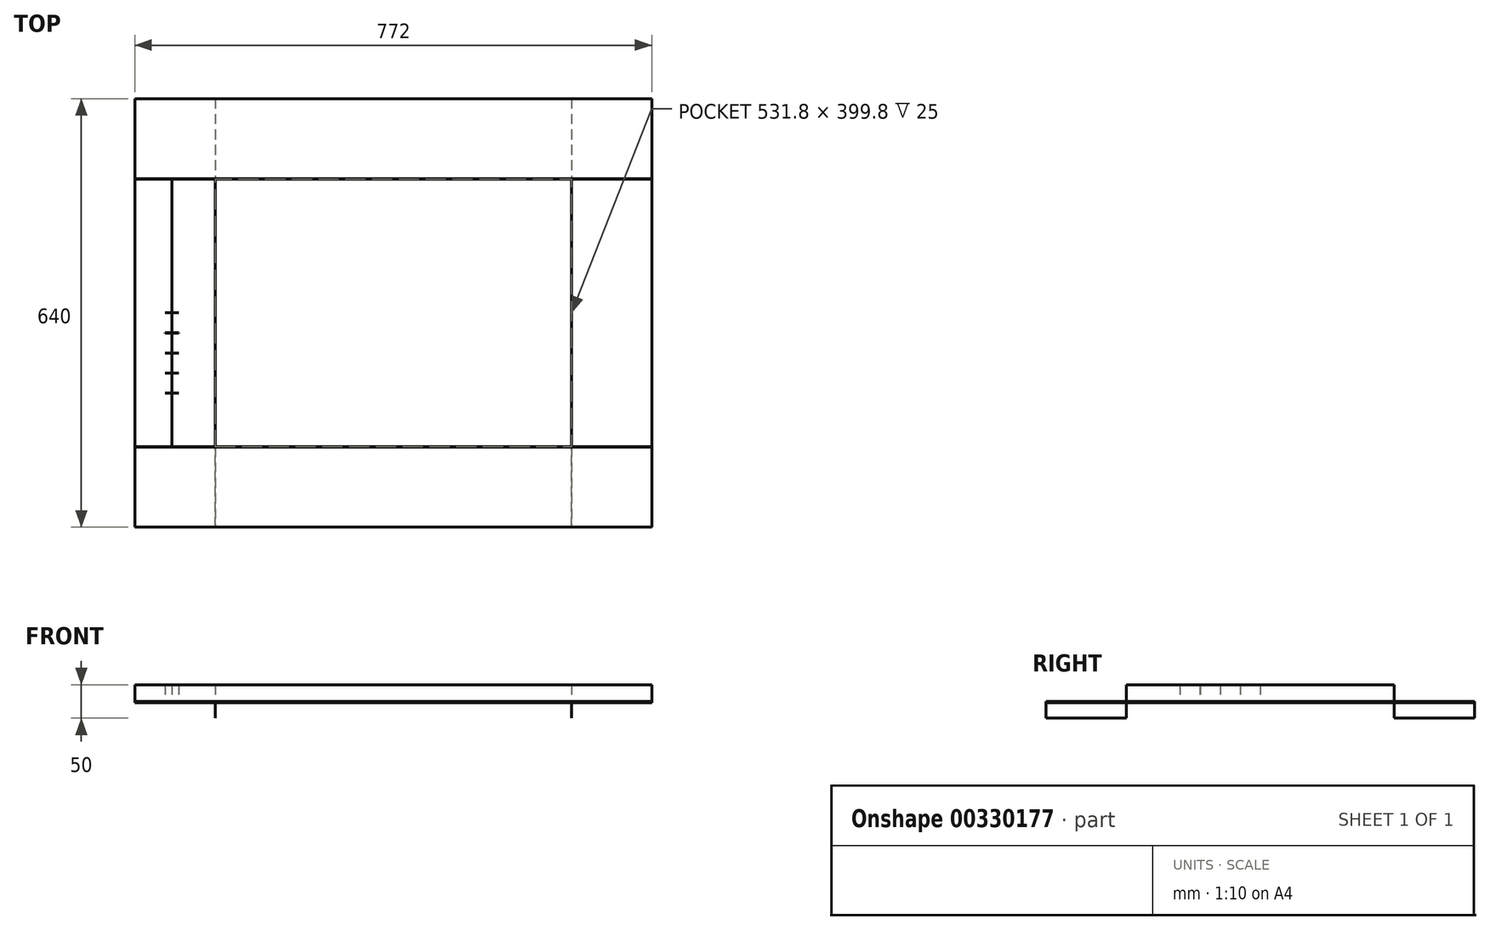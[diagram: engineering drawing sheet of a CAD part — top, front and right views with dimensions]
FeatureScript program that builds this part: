
annotation { "Feature Type Name" : "Feature", "Feature Type Description" : "" }
export const myFeature = defineFeature(function(context is Context, id is Id, definition is map)
    precondition{}
    {
        {
            var Q0;
            Q0=qCreatedBy(makeId("Top.planeOp"),FACE);
            var sketch = newSketch(context, id + "F0", { "sketchPlane" : qUnion([Q0])});
            skLineSegment(sketch, "E0.bottom", {"start": v(0, 0) * mm, "end": v(772, 0) * mm});
            skLineSegment(sketch, "E0.top", {"start": v(0, 640) * mm, "end": v(772, 640) * mm});
            skLineSegment(sketch, "E0.left", {"start": v(0, 0) * mm, "end": v(0, 640) * mm});
            skLineSegment(sketch, "E0.right", {"start": v(772, 0) * mm, "end": v(772, 640) * mm});
            skSolve(sketch);
        }
        {
            var Q0;
            Q0=makeQuery(id+"F0.imprint","IMPRINT",FACE,{"disambiguationData":[TD([[makeQuery(id+"F0.imprint","IMPRINT",EDGE,{"derivedFrom":sQuery(id+"F0.wireOp",EDGE,"E0.bottom")}),1.0]])]});
            extrude(context, id + "F1", {"entities" : qUnion([Q0]), "depth" : 2 * mm});
        }
        {
            var Q0;
            Q0=makeQuery(id+"F1.opExtrude","CAP_FACE",FACE,{"disambiguationData":[OSD([sQuery(id+"F0.wireOp",EDGE,"E0.bottom"),sQuery(id+"F0.wireOp",EDGE,"E0.top"),sQuery(id+"F0.wireOp",EDGE,"E0.left"),sQuery(id+"F0.wireOp",EDGE,"E0.right")])],"isStart":false});
            var sketch = newSketch(context, id + "F2", { "sketchPlane" : qUnion([Q0])});
            skLineSegment(sketch, "E1", {"start": v(0, 520.1) * mm, "end": v(772, 520.1) * mm});
            skLineSegment(sketch, "E2", {"start": v(0, 519.9) * mm, "end": v(772, 519.9) * mm});
            skLineSegment(sketch, "E3", {"start": v(0, 119.9) * mm, "end": v(772, 119.9) * mm});
            skLineSegment(sketch, "E4", {"start": v(0, 120.1) * mm, "end": v(772, 120.1) * mm});
            skLineSegment(sketch, "E5", {"start": v(652.1, 640) * mm, "end": v(652.1, 0) * mm});
            skLineSegment(sketch, "E6", {"start": v(119.9, 640) * mm, "end": v(119.9, 0) * mm});
            skLineSegment(sketch, "E7", {"start": v(120.1, 519.9) * mm, "end": v(120.1, 119.9) * mm});
            skLineSegment(sketch, "E8", {"start": v(651.9, 519.9) * mm, "end": v(651.9, 119.9) * mm});
            skLineSegment(sketch, "E9", {"start": v(120.15, 640) * mm, "end": v(120.15, 519.9) * mm});
            skLineSegment(sketch, "E10", {"start": v(651.85, 640) * mm, "end": v(651.85, 520.1) * mm});
            skLineSegment(sketch, "E11", {"start": v(120.15, 0) * mm, "end": v(120.15, 119.9) * mm});
            skLineSegment(sketch, "E12", {"start": v(651.85, 0) * mm, "end": v(651.85, 119.9) * mm});
            skLineSegment(sketch, "E13", {"start": v(55.2, 519.9) * mm, "end": v(55.2, 119.9) * mm});
            skLineSegment(sketch, "E14", {"start": v(55, 519.9) * mm, "end": v(55, 119.9) * mm});
            skLineSegment(sketch, "E15", {"start": v(45.2, 470.1) * mm, "end": v(45.2, 470.3) * mm});
            skLineSegment(sketch, "E16", {"start": v(65.2, 470.1) * mm, "end": v(65.2, 470.3) * mm});
            skLineSegment(sketch, "E17.1.0.2", {"start": v(65.2, 440.1) * mm, "end": v(65.2, 440.3) * mm});
            skLineSegment(sketch, "E17.1.0.3", {"start": v(45.2, 440.1) * mm, "end": v(45.2, 440.3) * mm});
            skLineSegment(sketch, "E17.2.0.2", {"start": v(65.2, 410.1) * mm, "end": v(65.2, 410.3) * mm});
            skLineSegment(sketch, "E17.2.0.3", {"start": v(45.2, 410.1) * mm, "end": v(45.2, 410.3) * mm});
            skLineSegment(sketch, "E17.3.0.2", {"start": v(65.2, 380.1) * mm, "end": v(65.2, 380.3) * mm});
            skLineSegment(sketch, "E17.3.0.3", {"start": v(45.2, 380.1) * mm, "end": v(45.2, 380.3) * mm});
            skLineSegment(sketch, "E17.4.0.2", {"start": v(65.2, 350.1) * mm, "end": v(65.2, 350.3) * mm});
            skLineSegment(sketch, "E17.4.0.3", {"start": v(45.2, 350.1) * mm, "end": v(45.2, 350.3) * mm});
            skLineSegment(sketch, "E17.5.0.2", {"start": v(65.2, 320.1) * mm, "end": v(65.2, 320.3) * mm});
            skLineSegment(sketch, "E17.5.0.3", {"start": v(45.2, 320.1) * mm, "end": v(45.2, 320.3) * mm});
            skLineSegment(sketch, "E17.6.0.2", {"start": v(65.2, 290.1) * mm, "end": v(65.2, 290.3) * mm});
            skLineSegment(sketch, "E17.6.0.3", {"start": v(45.2, 290.1) * mm, "end": v(45.2, 290.3) * mm});
            skLineSegment(sketch, "E17.7.0.2", {"start": v(65.2, 260.1) * mm, "end": v(65.2, 260.3) * mm});
            skLineSegment(sketch, "E17.7.0.3", {"start": v(45.2, 260.1) * mm, "end": v(45.2, 260.3) * mm});
            skLineSegment(sketch, "E17.8.0.2", {"start": v(65.2, 230.1) * mm, "end": v(65.2, 230.3) * mm});
            skLineSegment(sketch, "E17.8.0.3", {"start": v(45.2, 230.1) * mm, "end": v(45.2, 230.3) * mm});
            skLineSegment(sketch, "E17.9.0.2", {"start": v(65.2, 200.1) * mm, "end": v(65.2, 200.3) * mm});
            skLineSegment(sketch, "E17.9.0.3", {"start": v(45.2, 200.1) * mm, "end": v(45.2, 200.3) * mm});
            skLineSegment(sketch, "E17.direction1", {"start": v(45.2, 470.3) * mm, "end": v(45.2, 440.3) * mm, "construction": true});
            skLineSegment(sketch, "E18", {"start": v(55, 150.54) * mm, "end": v(55.2, 150.54) * mm});
            skLineSegment(sketch, "E19", {"start": v(45.2, 200.3) * mm, "end": v(65.2, 200.3) * mm});
            skLineSegment(sketch, "E20", {"start": v(45.2, 200.1) * mm, "end": v(65.2, 200.1) * mm});
            skLineSegment(sketch, "E21", {"start": v(45.2, 230.3) * mm, "end": v(65.2, 230.3) * mm});
            skLineSegment(sketch, "E22", {"start": v(65.2, 230.1) * mm, "end": v(45.2, 230.1) * mm});
            skLineSegment(sketch, "E23", {"start": v(45.2, 260.3) * mm, "end": v(65.2, 260.3) * mm});
            skLineSegment(sketch, "E24", {"start": v(65.2, 260.1) * mm, "end": v(45.2, 260.1) * mm});
            skLineSegment(sketch, "E25", {"start": v(45.2, 290.3) * mm, "end": v(65.2, 290.3) * mm});
            skLineSegment(sketch, "E26", {"start": v(65.2, 290.1) * mm, "end": v(45.2, 290.1) * mm});
            skLineSegment(sketch, "E27", {"start": v(45.2, 320.3) * mm, "end": v(65.2, 320.3) * mm});
            skLineSegment(sketch, "E28", {"start": v(45.2, 320.1) * mm, "end": v(65.2, 320.1) * mm});
            skSolve(sketch);
        }
        {
            var Q0;
            {var subQ0=sQuery(id+"F2.wireOp",EDGE,"E10");Q0=makeQuery(id+"F2.imprint","IMPRINT",FACE,{"disambiguationData":[TD([[makeQuery(id+"F2.imprint","IMPRINT",EDGE,{"derivedFrom":subQ0}),1.0]])]});}
            var Q1;
            {var subQ0=sQuery(id+"F2.wireOp",EDGE,"E6");var subQ1=sQuery(id+"F2.wireOp",EDGE,"E1");var subQ2=makeQuery(id+"F2.imprint","INTERSECT",VERTEX,{"derivedFrom":[subQ1,subQ0]});Q1=makeQuery(id+"F2.imprint","IMPRINT",FACE,{"disambiguationData":[TD([[makeQuery(id+"F2.imprint","IMPRINT",EDGE,{"disambiguationData":[TD([[subQ2,-1.0]])],"derivedFrom":subQ1}),1.0]])]});}
            var Q2;
            {var subQ0=sQuery(id+"F2.wireOp",EDGE,"E11");Q2=makeQuery(id+"F2.imprint","IMPRINT",FACE,{"disambiguationData":[TD([[makeQuery(id+"F2.imprint","IMPRINT",EDGE,{"derivedFrom":subQ0}),1.0]])]});}
            var Q3;
            {var subQ6=sQuery(id+"F2.wireOp",EDGE,"E12");Q3=makeQuery(id+"F2.imprint","IMPRINT",FACE,{"disambiguationData":[TD([[makeQuery(id+"F2.imprint","IMPRINT",EDGE,{"derivedFrom":subQ6}),-1.0]])]});}
            extrude(context, id + "F3", {"entities" : qUnion([Q0, Q1, Q2, Q3]), "operationType" : NewBodyOperationType.ADD, "oppositeDirection" : true, "depth" : 25 * mm});
        }
        {
            var Q0;
            {var subQ5=makeQuery(id+"F1.opExtrude","CAP_EDGE",EDGE,{"disambiguationData":[OSD([sQuery(id+"F0.wireOp",EDGE,"E0.left")])],"isStart":false});var subQ7=sQuery(id+"F2.wireOp",EDGE,"E1");var subQ8=makeQuery(id+"F2.imprint","INTERSECT",VERTEX,{"derivedFrom":[subQ5,subQ7]});Q0=makeQuery(id+"F2.imprint","IMPRINT",FACE,{"disambiguationData":[TD([[makeQuery(id+"F2.imprint","IMPRINT",EDGE,{"disambiguationData":[TD([[subQ8,-1.0]])],"derivedFrom":subQ7}),-1.0]])]});}
            var Q1;
            {var subQ6=sQuery(id+"F2.wireOp",EDGE,"E1");var subQ8=makeQuery(id+"F2.imprint","INTERSECT",VERTEX,{"derivedFrom":[subQ6,sQuery(id+"F2.wireOp",EDGE,"E10")]});Q1=makeQuery(id+"F2.imprint","IMPRINT",FACE,{"disambiguationData":[TD([[makeQuery(id+"F2.imprint","IMPRINT",EDGE,{"disambiguationData":[TD([[subQ8,1.0]])],"derivedFrom":subQ6}),-1.0]])]});}
            extrude(context, id + "F4", {"entities" : qUnion([Q0, Q1]), "operationType" : NewBodyOperationType.ADD, "depth" : 25 * mm});
        }
        {
            var Q0;
            {var subQ0=sQuery(id+"F2.wireOp",EDGE,"E1");var subQ1=makeQuery(id+"F1.opExtrude","CAP_EDGE",EDGE,{"disambiguationData":[OSD([sQuery(id+"F0.wireOp",EDGE,"E0.right")])],"isStart":false});var subQ2=makeQuery(id+"F2.imprint","INTERSECT",VERTEX,{"derivedFrom":[subQ1,subQ0]});Q0=makeQuery(id+"F2.imprint","IMPRINT",FACE,{"disambiguationData":[TD([[makeQuery(id+"F2.imprint","IMPRINT",EDGE,{"disambiguationData":[TD([[subQ2,1.0]])],"derivedFrom":subQ0}),-1.0]])]});}
            var Q1;
            {var subQ0=sQuery(id+"F2.wireOp",EDGE,"E8");var subQ1=sQuery(id+"F2.wireOp",EDGE,"E2");var subQ2=makeQuery(id+"F2.imprint","INTERSECT",VERTEX,{"derivedFrom":[subQ1,subQ0]});Q1=makeQuery(id+"F2.imprint","IMPRINT",FACE,{"disambiguationData":[TD([[makeQuery(id+"F2.imprint","IMPRINT",EDGE,{"disambiguationData":[TD([[subQ2,-1.0]])],"derivedFrom":subQ1}),-1.0]])]});}
            extrude(context, id + "F5", {"entities" : qUnion([Q0, Q1]), "operationType" : NewBodyOperationType.ADD, "depth" : 25 * mm});
        }
        {
            var Q0;
            {var subQ0=sQuery(id+"F2.wireOp",EDGE,"E3");var subQ1=makeQuery(id+"F1.opExtrude","CAP_EDGE",EDGE,{"disambiguationData":[OSD([sQuery(id+"F0.wireOp",EDGE,"E0.right")])],"isStart":false});var subQ2=makeQuery(id+"F2.imprint","INTERSECT",VERTEX,{"derivedFrom":[subQ1,subQ0]});Q0=makeQuery(id+"F2.imprint","IMPRINT",FACE,{"disambiguationData":[TD([[makeQuery(id+"F2.imprint","IMPRINT",EDGE,{"disambiguationData":[TD([[subQ2,1.0]])],"derivedFrom":subQ0}),1.0]])]});}
            var Q1;
            {var subQ0=sQuery(id+"F2.wireOp",EDGE,"E7");var subQ5=sQuery(id+"F2.wireOp",EDGE,"E3");var subQ9=makeQuery(id+"F2.imprint","INTERSECT",VERTEX,{"derivedFrom":[subQ5,subQ0]});Q1=makeQuery(id+"F2.imprint","IMPRINT",FACE,{"disambiguationData":[TD([[makeQuery(id+"F2.imprint","IMPRINT",EDGE,{"disambiguationData":[TD([[subQ9,-1.0]])],"derivedFrom":subQ5}),1.0]])]});}
            var Q2;
            {var subQ0=sQuery(id+"F2.wireOp",EDGE,"E8");var subQ1=sQuery(id+"F2.wireOp",EDGE,"E3");var subQ2=makeQuery(id+"F2.imprint","INTERSECT",VERTEX,{"derivedFrom":[subQ1,subQ0]});Q2=makeQuery(id+"F2.imprint","IMPRINT",FACE,{"disambiguationData":[TD([[makeQuery(id+"F2.imprint","IMPRINT",EDGE,{"disambiguationData":[TD([[subQ2,-1.0]])],"derivedFrom":subQ1}),1.0]])]});}
            var Q3;
            {var subQ0=sQuery(id+"F2.wireOp",EDGE,"E13");var subQ1=sQuery(id+"F2.wireOp",EDGE,"E3");var subQ2=makeQuery(id+"F2.imprint","INTERSECT",VERTEX,{"derivedFrom":[subQ1,subQ0]});Q3=makeQuery(id+"F2.imprint","IMPRINT",FACE,{"disambiguationData":[TD([[makeQuery(id+"F2.imprint","IMPRINT",EDGE,{"disambiguationData":[TD([[subQ2,-1.0]])],"derivedFrom":subQ1}),1.0]])]});}
            var Q4;
            {var subQ0=sQuery(id+"F2.wireOp",EDGE,"E7");var subQ1=sQuery(id+"F2.wireOp",EDGE,"E3");var subQ2=makeQuery(id+"F2.imprint","INTERSECT",VERTEX,{"derivedFrom":[subQ1,subQ0]});Q4=makeQuery(id+"F2.imprint","IMPRINT",FACE,{"disambiguationData":[TD([[makeQuery(id+"F2.imprint","IMPRINT",EDGE,{"disambiguationData":[TD([[subQ2,1.0]])],"derivedFrom":subQ1}),1.0]])]});}
            extrude(context, id + "F6", {"entities" : qUnion([Q0, Q1, Q2, Q3, Q4]), "operationType" : NewBodyOperationType.ADD, "depth" : 25 * mm});
        }
        {
            var Q0;
            {var subQ0=sQuery(id+"F2.wireOp",EDGE,"E3");var subQ1=makeQuery(id+"F1.opExtrude","CAP_EDGE",EDGE,{"disambiguationData":[OSD([sQuery(id+"F0.wireOp",EDGE,"E0.left")])],"isStart":false});var subQ2=makeQuery(id+"F2.imprint","INTERSECT",VERTEX,{"derivedFrom":[subQ1,subQ0]});Q0=makeQuery(id+"F2.imprint","IMPRINT",FACE,{"disambiguationData":[TD([[makeQuery(id+"F2.imprint","IMPRINT",EDGE,{"disambiguationData":[TD([[subQ2,-1.0]])],"derivedFrom":subQ0}),1.0]])]});}
            extrude(context, id + "F7", {"entities" : qUnion([Q0]), "operationType" : NewBodyOperationType.ADD, "depth" : 25 * mm});
        }
        {
            var Q0;
            {var subQ0=sQuery(id+"F2.wireOp",EDGE,"E18");Q0=makeQuery(id+"F2.imprint","IMPRINT",FACE,{"disambiguationData":[TD([[makeQuery(id+"F2.imprint","IMPRINT",EDGE,{"derivedFrom":subQ0}),1.0]])]});}
            extrude(context, id + "F8", {"entities" : qUnion([Q0]), "operationType" : NewBodyOperationType.ADD, "depth" : 25 * mm});
        }
        {
            var Q0;
            {var subQ0=sQuery(id+"F2.wireOp",EDGE,"E18");Q0=makeQuery(id+"F2.imprint","IMPRINT",FACE,{"disambiguationData":[TD([[makeQuery(id+"F2.imprint","IMPRINT",EDGE,{"derivedFrom":subQ0}),1.0]])]});}
            var Q1;
            {var subQ5=sQuery(id+"F2.wireOp",EDGE,"E17.9.0.3");Q1=makeQuery(id+"F2.imprint","IMPRINT",FACE,{"disambiguationData":[TD([[makeQuery(id+"F2.imprint","IMPRINT",EDGE,{"derivedFrom":subQ5}),-1.0]])]});}
            var Q2;
            {var subQ5=sQuery(id+"F2.wireOp",EDGE,"E17.9.0.2");Q2=makeQuery(id+"F2.imprint","IMPRINT",FACE,{"disambiguationData":[TD([[makeQuery(id+"F2.imprint","IMPRINT",EDGE,{"derivedFrom":subQ5}),1.0]])]});}
            var Q3;
            {var subQ0=sQuery(id+"F2.wireOp",EDGE,"E17.8.0.0");var subQ1=sQuery(id+"F2.wireOp",EDGE,"E13");var subQ2=makeQuery(id+"F2.imprint","INTERSECT",VERTEX,{"derivedFrom":[subQ1,subQ0]});Q3=makeQuery(id+"F2.imprint","IMPRINT",FACE,{"disambiguationData":[TD([[makeQuery(id+"F2.imprint","IMPRINT",EDGE,{"disambiguationData":[TD([[subQ2,-1.0]])],"derivedFrom":subQ1}),-1.0]])]});}
            var Q4;
            {var subQ0=sQuery(id+"F2.wireOp",EDGE,"E17.9.0.1");var subQ1=sQuery(id+"F2.wireOp",EDGE,"E13");var subQ2=makeQuery(id+"F2.imprint","INTERSECT",VERTEX,{"derivedFrom":[subQ1,subQ0]});Q4=makeQuery(id+"F2.imprint","IMPRINT",FACE,{"disambiguationData":[TD([[makeQuery(id+"F2.imprint","IMPRINT",EDGE,{"disambiguationData":[TD([[subQ2,-1.0]])],"derivedFrom":subQ1}),-1.0]])]});}
            var Q5;
            {var subQ5=sQuery(id+"F2.wireOp",EDGE,"E17.8.0.3");Q5=makeQuery(id+"F2.imprint","IMPRINT",FACE,{"disambiguationData":[TD([[makeQuery(id+"F2.imprint","IMPRINT",EDGE,{"derivedFrom":subQ5}),-1.0]])]});}
            var Q6;
            {var subQ5=sQuery(id+"F2.wireOp",EDGE,"E17.8.0.2");Q6=makeQuery(id+"F2.imprint","IMPRINT",FACE,{"disambiguationData":[TD([[makeQuery(id+"F2.imprint","IMPRINT",EDGE,{"derivedFrom":subQ5}),1.0]])]});}
            var Q7;
            {var subQ0=sQuery(id+"F2.wireOp",EDGE,"E17.8.0.1");var subQ1=sQuery(id+"F2.wireOp",EDGE,"E13");var subQ2=makeQuery(id+"F2.imprint","INTERSECT",VERTEX,{"derivedFrom":[subQ1,subQ0]});Q7=makeQuery(id+"F2.imprint","IMPRINT",FACE,{"disambiguationData":[TD([[makeQuery(id+"F2.imprint","IMPRINT",EDGE,{"disambiguationData":[TD([[subQ2,-1.0]])],"derivedFrom":subQ1}),-1.0]])]});}
            var Q8;
            {var subQ0=sQuery(id+"F2.wireOp",EDGE,"E17.7.0.0");var subQ1=sQuery(id+"F2.wireOp",EDGE,"E13");var subQ2=makeQuery(id+"F2.imprint","INTERSECT",VERTEX,{"derivedFrom":[subQ1,subQ0]});Q8=makeQuery(id+"F2.imprint","IMPRINT",FACE,{"disambiguationData":[TD([[makeQuery(id+"F2.imprint","IMPRINT",EDGE,{"disambiguationData":[TD([[subQ2,-1.0]])],"derivedFrom":subQ1}),-1.0]])]});}
            var Q9;
            {var subQ5=sQuery(id+"F2.wireOp",EDGE,"E17.7.0.3");Q9=makeQuery(id+"F2.imprint","IMPRINT",FACE,{"disambiguationData":[TD([[makeQuery(id+"F2.imprint","IMPRINT",EDGE,{"derivedFrom":subQ5}),-1.0]])]});}
            var Q10;
            {var subQ5=sQuery(id+"F2.wireOp",EDGE,"E17.7.0.2");Q10=makeQuery(id+"F2.imprint","IMPRINT",FACE,{"disambiguationData":[TD([[makeQuery(id+"F2.imprint","IMPRINT",EDGE,{"derivedFrom":subQ5}),1.0]])]});}
            var Q11;
            {var subQ0=sQuery(id+"F2.wireOp",EDGE,"E17.7.0.1");var subQ1=sQuery(id+"F2.wireOp",EDGE,"E13");var subQ2=makeQuery(id+"F2.imprint","INTERSECT",VERTEX,{"derivedFrom":[subQ1,subQ0]});Q11=makeQuery(id+"F2.imprint","IMPRINT",FACE,{"disambiguationData":[TD([[makeQuery(id+"F2.imprint","IMPRINT",EDGE,{"disambiguationData":[TD([[subQ2,-1.0]])],"derivedFrom":subQ1}),-1.0]])]});}
            var Q12;
            {var subQ0=sQuery(id+"F2.wireOp",EDGE,"E17.6.0.0");var subQ1=sQuery(id+"F2.wireOp",EDGE,"E13");var subQ2=makeQuery(id+"F2.imprint","INTERSECT",VERTEX,{"derivedFrom":[subQ1,subQ0]});Q12=makeQuery(id+"F2.imprint","IMPRINT",FACE,{"disambiguationData":[TD([[makeQuery(id+"F2.imprint","IMPRINT",EDGE,{"disambiguationData":[TD([[subQ2,-1.0]])],"derivedFrom":subQ1}),-1.0]])]});}
            var Q13;
            {var subQ5=sQuery(id+"F2.wireOp",EDGE,"E17.6.0.3");Q13=makeQuery(id+"F2.imprint","IMPRINT",FACE,{"disambiguationData":[TD([[makeQuery(id+"F2.imprint","IMPRINT",EDGE,{"derivedFrom":subQ5}),-1.0]])]});}
            var Q14;
            {var subQ5=sQuery(id+"F2.wireOp",EDGE,"E17.6.0.2");Q14=makeQuery(id+"F2.imprint","IMPRINT",FACE,{"disambiguationData":[TD([[makeQuery(id+"F2.imprint","IMPRINT",EDGE,{"derivedFrom":subQ5}),1.0]])]});}
            var Q15;
            {var subQ0=sQuery(id+"F2.wireOp",EDGE,"E17.6.0.1");var subQ1=sQuery(id+"F2.wireOp",EDGE,"E13");var subQ2=makeQuery(id+"F2.imprint","INTERSECT",VERTEX,{"derivedFrom":[subQ1,subQ0]});Q15=makeQuery(id+"F2.imprint","IMPRINT",FACE,{"disambiguationData":[TD([[makeQuery(id+"F2.imprint","IMPRINT",EDGE,{"disambiguationData":[TD([[subQ2,-1.0]])],"derivedFrom":subQ1}),-1.0]])]});}
            var Q16;
            {var subQ0=sQuery(id+"F2.wireOp",EDGE,"E17.5.0.0");var subQ1=sQuery(id+"F2.wireOp",EDGE,"E13");var subQ2=makeQuery(id+"F2.imprint","INTERSECT",VERTEX,{"derivedFrom":[subQ1,subQ0]});Q16=makeQuery(id+"F2.imprint","IMPRINT",FACE,{"disambiguationData":[TD([[makeQuery(id+"F2.imprint","IMPRINT",EDGE,{"disambiguationData":[TD([[subQ2,-1.0]])],"derivedFrom":subQ1}),-1.0]])]});}
            var Q17;
            {var subQ5=sQuery(id+"F2.wireOp",EDGE,"E17.5.0.3");Q17=makeQuery(id+"F2.imprint","IMPRINT",FACE,{"disambiguationData":[TD([[makeQuery(id+"F2.imprint","IMPRINT",EDGE,{"derivedFrom":subQ5}),-1.0]])]});}
            var Q18;
            {var subQ0=sQuery(id+"F2.wireOp",EDGE,"E17.5.0.1");var subQ1=sQuery(id+"F2.wireOp",EDGE,"E13");var subQ2=makeQuery(id+"F2.imprint","INTERSECT",VERTEX,{"derivedFrom":[subQ1,subQ0]});Q18=makeQuery(id+"F2.imprint","IMPRINT",FACE,{"disambiguationData":[TD([[makeQuery(id+"F2.imprint","IMPRINT",EDGE,{"disambiguationData":[TD([[subQ2,-1.0]])],"derivedFrom":subQ1}),-1.0]])]});}
            var Q19;
            {var subQ5=sQuery(id+"F2.wireOp",EDGE,"E17.5.0.2");Q19=makeQuery(id+"F2.imprint","IMPRINT",FACE,{"disambiguationData":[TD([[makeQuery(id+"F2.imprint","IMPRINT",EDGE,{"derivedFrom":subQ5}),1.0]])]});}
            var Q20;
            {var subQ0=sQuery(id+"F2.wireOp",EDGE,"E17.4.0.0");var subQ1=sQuery(id+"F2.wireOp",EDGE,"E13");var subQ2=makeQuery(id+"F2.imprint","INTERSECT",VERTEX,{"derivedFrom":[subQ1,subQ0]});Q20=makeQuery(id+"F2.imprint","IMPRINT",FACE,{"disambiguationData":[TD([[makeQuery(id+"F2.imprint","IMPRINT",EDGE,{"disambiguationData":[TD([[subQ2,-1.0]])],"derivedFrom":subQ1}),-1.0]])]});}
            var Q21;
            {var subQ5=sQuery(id+"F2.wireOp",EDGE,"E17.4.0.3");Q21=makeQuery(id+"F2.imprint","IMPRINT",FACE,{"disambiguationData":[TD([[makeQuery(id+"F2.imprint","IMPRINT",EDGE,{"derivedFrom":subQ5}),-1.0]])]});}
            var Q22;
            {var subQ0=sQuery(id+"F2.wireOp",EDGE,"E17.4.0.1");var subQ1=sQuery(id+"F2.wireOp",EDGE,"E13");var subQ2=makeQuery(id+"F2.imprint","INTERSECT",VERTEX,{"derivedFrom":[subQ1,subQ0]});Q22=makeQuery(id+"F2.imprint","IMPRINT",FACE,{"disambiguationData":[TD([[makeQuery(id+"F2.imprint","IMPRINT",EDGE,{"disambiguationData":[TD([[subQ2,-1.0]])],"derivedFrom":subQ1}),-1.0]])]});}
            var Q23;
            {var subQ5=sQuery(id+"F2.wireOp",EDGE,"E17.4.0.2");Q23=makeQuery(id+"F2.imprint","IMPRINT",FACE,{"disambiguationData":[TD([[makeQuery(id+"F2.imprint","IMPRINT",EDGE,{"derivedFrom":subQ5}),1.0]])]});}
            var Q24;
            {var subQ0=sQuery(id+"F2.wireOp",EDGE,"E17.3.0.0");var subQ1=sQuery(id+"F2.wireOp",EDGE,"E13");var subQ2=makeQuery(id+"F2.imprint","INTERSECT",VERTEX,{"derivedFrom":[subQ1,subQ0]});Q24=makeQuery(id+"F2.imprint","IMPRINT",FACE,{"disambiguationData":[TD([[makeQuery(id+"F2.imprint","IMPRINT",EDGE,{"disambiguationData":[TD([[subQ2,-1.0]])],"derivedFrom":subQ1}),-1.0]])]});}
            var Q25;
            {var subQ5=sQuery(id+"F2.wireOp",EDGE,"E17.3.0.3");Q25=makeQuery(id+"F2.imprint","IMPRINT",FACE,{"disambiguationData":[TD([[makeQuery(id+"F2.imprint","IMPRINT",EDGE,{"derivedFrom":subQ5}),-1.0]])]});}
            var Q26;
            {var subQ0=sQuery(id+"F2.wireOp",EDGE,"E17.3.0.1");var subQ1=sQuery(id+"F2.wireOp",EDGE,"E13");var subQ2=makeQuery(id+"F2.imprint","INTERSECT",VERTEX,{"derivedFrom":[subQ1,subQ0]});Q26=makeQuery(id+"F2.imprint","IMPRINT",FACE,{"disambiguationData":[TD([[makeQuery(id+"F2.imprint","IMPRINT",EDGE,{"disambiguationData":[TD([[subQ2,-1.0]])],"derivedFrom":subQ1}),-1.0]])]});}
            var Q27;
            {var subQ5=sQuery(id+"F2.wireOp",EDGE,"E17.3.0.2");Q27=makeQuery(id+"F2.imprint","IMPRINT",FACE,{"disambiguationData":[TD([[makeQuery(id+"F2.imprint","IMPRINT",EDGE,{"derivedFrom":subQ5}),1.0]])]});}
            var Q28;
            {var subQ0=sQuery(id+"F2.wireOp",EDGE,"E17.2.0.0");var subQ1=sQuery(id+"F2.wireOp",EDGE,"E13");var subQ2=makeQuery(id+"F2.imprint","INTERSECT",VERTEX,{"derivedFrom":[subQ1,subQ0]});Q28=makeQuery(id+"F2.imprint","IMPRINT",FACE,{"disambiguationData":[TD([[makeQuery(id+"F2.imprint","IMPRINT",EDGE,{"disambiguationData":[TD([[subQ2,-1.0]])],"derivedFrom":subQ1}),-1.0]])]});}
            var Q29;
            {var subQ5=sQuery(id+"F2.wireOp",EDGE,"E17.2.0.3");Q29=makeQuery(id+"F2.imprint","IMPRINT",FACE,{"disambiguationData":[TD([[makeQuery(id+"F2.imprint","IMPRINT",EDGE,{"derivedFrom":subQ5}),-1.0]])]});}
            var Q30;
            {var subQ0=sQuery(id+"F2.wireOp",EDGE,"E17.2.0.1");var subQ1=sQuery(id+"F2.wireOp",EDGE,"E13");var subQ2=makeQuery(id+"F2.imprint","INTERSECT",VERTEX,{"derivedFrom":[subQ1,subQ0]});Q30=makeQuery(id+"F2.imprint","IMPRINT",FACE,{"disambiguationData":[TD([[makeQuery(id+"F2.imprint","IMPRINT",EDGE,{"disambiguationData":[TD([[subQ2,-1.0]])],"derivedFrom":subQ1}),-1.0]])]});}
            var Q31;
            {var subQ5=sQuery(id+"F2.wireOp",EDGE,"E17.2.0.2");Q31=makeQuery(id+"F2.imprint","IMPRINT",FACE,{"disambiguationData":[TD([[makeQuery(id+"F2.imprint","IMPRINT",EDGE,{"derivedFrom":subQ5}),1.0]])]});}
            var Q32;
            {var subQ0=sQuery(id+"F2.wireOp",EDGE,"E17.1.0.0");var subQ1=sQuery(id+"F2.wireOp",EDGE,"E13");var subQ2=makeQuery(id+"F2.imprint","INTERSECT",VERTEX,{"derivedFrom":[subQ1,subQ0]});Q32=makeQuery(id+"F2.imprint","IMPRINT",FACE,{"disambiguationData":[TD([[makeQuery(id+"F2.imprint","IMPRINT",EDGE,{"disambiguationData":[TD([[subQ2,-1.0]])],"derivedFrom":subQ1}),-1.0]])]});}
            var Q33;
            {var subQ5=sQuery(id+"F2.wireOp",EDGE,"E17.1.0.3");Q33=makeQuery(id+"F2.imprint","IMPRINT",FACE,{"disambiguationData":[TD([[makeQuery(id+"F2.imprint","IMPRINT",EDGE,{"derivedFrom":subQ5}),-1.0]])]});}
            var Q34;
            {var subQ0=sQuery(id+"F2.wireOp",EDGE,"E17.1.0.1");var subQ1=sQuery(id+"F2.wireOp",EDGE,"E13");var subQ2=makeQuery(id+"F2.imprint","INTERSECT",VERTEX,{"derivedFrom":[subQ1,subQ0]});Q34=makeQuery(id+"F2.imprint","IMPRINT",FACE,{"disambiguationData":[TD([[makeQuery(id+"F2.imprint","IMPRINT",EDGE,{"disambiguationData":[TD([[subQ2,-1.0]])],"derivedFrom":subQ1}),-1.0]])]});}
            var Q35;
            {var subQ5=sQuery(id+"F2.wireOp",EDGE,"E17.1.0.2");Q35=makeQuery(id+"F2.imprint","IMPRINT",FACE,{"disambiguationData":[TD([[makeQuery(id+"F2.imprint","IMPRINT",EDGE,{"derivedFrom":subQ5}),1.0]])]});}
            var Q36;
            {var subQ0=sQuery(id+"F2.wireOp",EDGE,"PF9Whc2X-JOV0-p4xt-AjMA-3nAZ7eqoeYj6");var subQ1=sQuery(id+"F2.wireOp",EDGE,"E13");var subQ2=makeQuery(id+"F2.imprint","INTERSECT",VERTEX,{"derivedFrom":[subQ1,subQ0]});Q36=makeQuery(id+"F2.imprint","IMPRINT",FACE,{"disambiguationData":[TD([[makeQuery(id+"F2.imprint","IMPRINT",EDGE,{"disambiguationData":[TD([[subQ2,-1.0]])],"derivedFrom":subQ1}),-1.0]])]});}
            var Q37;
            {var subQ5=sQuery(id+"F2.wireOp",EDGE,"E15");Q37=makeQuery(id+"F2.imprint","IMPRINT",FACE,{"disambiguationData":[TD([[makeQuery(id+"F2.imprint","IMPRINT",EDGE,{"derivedFrom":subQ5}),-1.0]])]});}
            var Q38;
            {var subQ0=sQuery(id+"F2.wireOp",EDGE,"TrYL828V-23KU-50iI-e81v-BixSrFEmtcK7");var subQ1=sQuery(id+"F2.wireOp",EDGE,"E13");var subQ2=makeQuery(id+"F2.imprint","INTERSECT",VERTEX,{"derivedFrom":[subQ1,subQ0]});Q38=makeQuery(id+"F2.imprint","IMPRINT",FACE,{"disambiguationData":[TD([[makeQuery(id+"F2.imprint","IMPRINT",EDGE,{"disambiguationData":[TD([[subQ2,-1.0]])],"derivedFrom":subQ1}),-1.0]])]});}
            var Q39;
            {var subQ5=sQuery(id+"F2.wireOp",EDGE,"E16");Q39=makeQuery(id+"F2.imprint","IMPRINT",FACE,{"disambiguationData":[TD([[makeQuery(id+"F2.imprint","IMPRINT",EDGE,{"derivedFrom":subQ5}),1.0]])]});}
            var Q40;
            {var subQ0=sQuery(id+"F2.wireOp",EDGE,"E13");var subQ1=sQuery(id+"F2.wireOp",EDGE,"E2");var subQ2=makeQuery(id+"F2.imprint","INTERSECT",VERTEX,{"derivedFrom":[subQ1,subQ0]});Q40=makeQuery(id+"F2.imprint","IMPRINT",FACE,{"disambiguationData":[TD([[makeQuery(id+"F2.imprint","IMPRINT",EDGE,{"disambiguationData":[TD([[subQ2,1.0]])],"derivedFrom":subQ1}),-1.0]])]});}
            var Q41;
            {var subQ0=sQuery(id+"F2.wireOp",EDGE,"E7");var subQ1=sQuery(id+"F2.wireOp",EDGE,"E2");var subQ2=makeQuery(id+"F2.imprint","INTERSECT",VERTEX,{"derivedFrom":[subQ1,subQ0]});Q41=makeQuery(id+"F2.imprint","IMPRINT",FACE,{"disambiguationData":[TD([[makeQuery(id+"F2.imprint","IMPRINT",EDGE,{"disambiguationData":[TD([[subQ2,1.0]])],"derivedFrom":subQ1}),-1.0]])]});}
            var Q42;
            {var subQ0=sQuery(id+"F2.wireOp",EDGE,"E6");var subQ1=sQuery(id+"F2.wireOp",EDGE,"E1");var subQ2=makeQuery(id+"F2.imprint","INTERSECT",VERTEX,{"derivedFrom":[subQ1,subQ0]});Q42=makeQuery(id+"F2.imprint","IMPRINT",FACE,{"disambiguationData":[TD([[makeQuery(id+"F2.imprint","IMPRINT",EDGE,{"disambiguationData":[TD([[subQ2,-1.0]])],"derivedFrom":subQ1}),-1.0]])]});}
            var Q43;
            {var subQ5=sQuery(id+"F2.wireOp",EDGE,"E18");Q43=makeQuery(id+"F2.imprint","IMPRINT",FACE,{"disambiguationData":[TD([[makeQuery(id+"F2.imprint","IMPRINT",EDGE,{"derivedFrom":subQ5}),-1.0]])]});}
            var Q44;
            {var subQ0=sQuery(id+"F2.wireOp",EDGE,"E13");var subQ1=sQuery(id+"F2.wireOp",EDGE,"E3");var subQ2=makeQuery(id+"F2.imprint","INTERSECT",VERTEX,{"derivedFrom":[subQ1,subQ0]});Q44=makeQuery(id+"F2.imprint","IMPRINT",FACE,{"disambiguationData":[TD([[makeQuery(id+"F2.imprint","IMPRINT",EDGE,{"disambiguationData":[TD([[subQ2,1.0]])],"derivedFrom":subQ1}),1.0]])]});}
            extrude(context, id + "F9", {"entities" : qUnion([Q0, Q1, Q2, Q3, Q4, Q5, Q6, Q7, Q8, Q9, Q10, Q11, Q12, Q13, Q14, Q15, Q16, Q17, Q18, Q19, Q20, Q21, Q22, Q23, Q24, Q25, Q26, Q27, Q28, Q29, Q30, Q31, Q32, Q33, Q34, Q35, Q36, Q37, Q38, Q39, Q40, Q41, Q42, Q43, Q44]), "operationType" : NewBodyOperationType.ADD, "depth" : 25 * mm});
        }
    });
